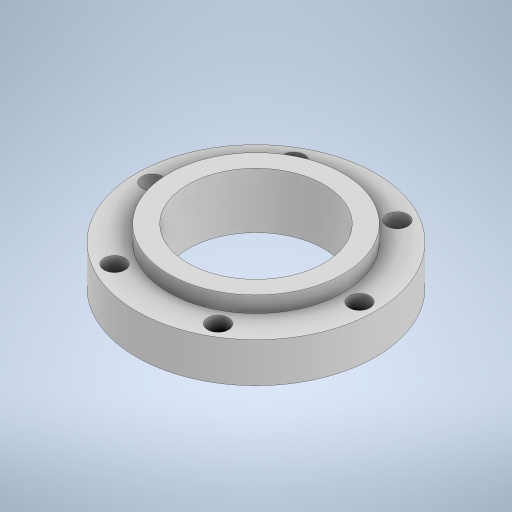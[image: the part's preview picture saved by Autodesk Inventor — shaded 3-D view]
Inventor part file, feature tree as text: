
AUTODESK INVENTOR PART (.ipt)
format: ipt  version: 2024 (Build 280153000, 153)  size: 271,360 bytes
history: native  units: mm
features: extrude x2, sketch x2
ambient origin geometry x8: Origin, YZ Plane, XZ Plane, XY Plane, X Axis, Y Axis, Z Axis, Center Point
bodies: Solid1 (feature_tree)
feature tree (4):
  extrude  "Extrusion1"  Depth=5.0mm TaperAngle=0.0deg
  extrude  "Extrusion2"  Depth=2.0mm TaperAngle=0.0deg
  sketch  "Sketch1"  dims[d1=60.0mm d2=2.6mm d3=13.0mm d4=360.0deg d5=5.0mm d6=0.0mm]
  sketch  "Sketch2"  dims[d7=21.9mm d8=2.0mm d9=0.0mm]
